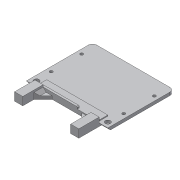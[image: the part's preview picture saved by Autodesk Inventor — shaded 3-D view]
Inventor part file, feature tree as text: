
AUTODESK INVENTOR PART (.ipt)
format: ipt  version: 2013 (Build 170138000, 138)  size: 184,320 bytes
history: native  units: mm
features: chamfer x7, hole x6, extrude x4, sketch x4, fillet x2
ambient origin geometry x8: Origin, YZ Plane, XZ Plane, XY Plane, X Axis, Y Axis, Z Axis, Center Point
feature tree (23):
  extrude  "Extrusion2"  Depth=65.0mm
  extrude  "Extrusion5"  Depth=8.0mm
  chamfer  "Fase3"  Distance=20.0mm
  chamfer  "Fase4"  Distance=8.0mm
  chamfer  "Fase5"  Distance=9.0mm Angle=45.0deg
  chamfer  "Fase6"  Distance=9.0mm Angle=45.0deg
  fillet  "Rundung17"  Radius=3.0mm
  extrude  "Extrusion13"  Depth=3.0mm TaperAngle=45.0deg
  extrude  "Extrusion15"  Depth=4.0mm
  fillet  "Rundung19"  Radius=1.0mm
  chamfer  "Fase13"  Distance=40.0mm
  chamfer  "Fase14"  Distance=2.0mm
  hole  "Bohrung5"  [1 undecoded]
  hole  "Bohrung6"  [1 undecoded]
  hole  "Bohrung7"  [1 undecoded]
  hole  "Bohrung8"  [1 undecoded]
  hole  "Bohrung9"  [1 undecoded]
  hole  "Bohrung10"  [1 undecoded]
  chamfer  "Fase16"  Distance=60.0mm
  sketch  "Skizze1"  dims[d0=80.0mm d1=65.0mm]
  sketch  "Skizze5"  dims[d32=3.0mm d33=0.0mm d105=8.0mm]
  sketch  "Skizze13"  dims[d108=63.0mm]
  sketch  "Skizze15"  dims[d109=8.5mm d110=20.0mm d111=0.0mm d112=8.0mm d121=9.0mm d122=7.0mm d123=45.0deg d124=9.0mm d125=7.0mm d126=45.0deg d127=3.0mm d128=7.0mm d129=45.0deg d130=3.0mm d131=7.0mm d132=45.0deg d181=4.0mm d182=1.0mm d183=0.0mm d189=40.0mm d190=2.0mm d191=10.0mm d192=2.0mm d193=0.0mm d194=1.0mm d195=2.9999mm d196=7.0mm d197=6.981317mm d198=2.9999mm d199=7.0mm d200=6.981317mm d202=5.0mm d203=5.0mm d204=5.0mm d205=6.0mm d206=4.0mm d207=2.0mm d208=90.0deg d209=8.0mm d210=20.594885mm d211=5.0mm d212=5.0mm d213=5.0mm d214=6.0mm d215=4.0mm d216=2.0mm d217=90.0deg d218=8.0mm d219=20.594885mm d220=4.35mm d221=10.0mm d222=3.0mm d223=6.0mm d224=4.0mm d225=2.0mm d226=90.0deg d227=8.0mm d228=20.594885mm d229=4.35mm d230=40.0mm d231=3.0mm d232=6.0mm d233=4.0mm d234=2.0mm d235=90.0deg d236=8.0mm d237=20.594885mm d238=4.35mm d239=10.0mm d240=3.0mm d241=6.0mm d242=4.0mm d243=2.0mm d244=90.0deg d245=8.0mm d246=20.594885mm d247=4.35mm d248=40.0mm d249=3.0mm d250=6.0mm d251=4.0mm d252=2.0mm d253=90.0deg d254=8.0mm d255=20.594885mm d257=60.0mm d258=10.0mm d259=10.0mm d263=2.0mm d264=2.0mm d265=45.0deg d4=1.0mm d5=1.0mm]
note: 6 required parameter values undecoded (feature->parameter linkage not recoverable at this tier; creation-order binding heuristic only, values carry confidence <= 0.55)
